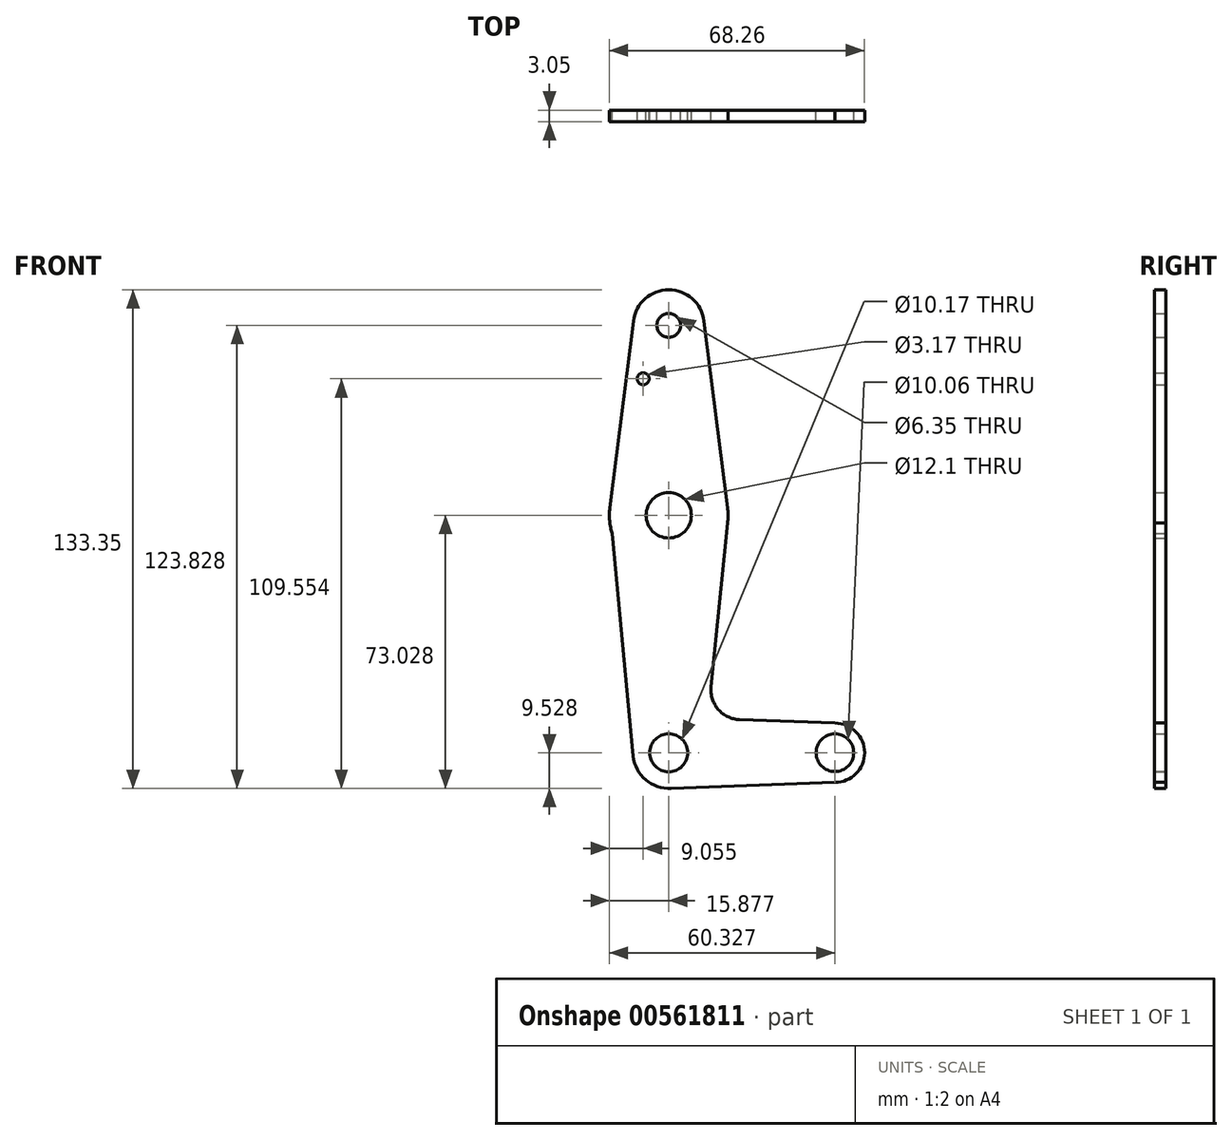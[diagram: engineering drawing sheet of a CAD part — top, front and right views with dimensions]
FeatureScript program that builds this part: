
annotation { "Feature Type Name" : "Feature", "Feature Type Description" : "" }
export const myFeature = defineFeature(function(context is Context, id is Id, definition is map)
    precondition{}
    {
        {
            var Q0;
            Q0=qCreatedBy(makeId("Front.planeOp"),FACE);
            var sketch = newSketch(context, id + "F0", { "sketchPlane" : qUnion([Q0])});
            skLineSegment(sketch, "E0", {"start": v(-18.2, 57.07) * mm, "end": v(-18.2, -57.23) * mm, "construction": true});
            skLineSegment(sketch, "E1", {"start": v(-18.2, -57.23) * mm, "end": v(26.26, -57.23) * mm, "construction": true});
            skCircle(sketch, "E2", {"center": v(-18.2, 57.07) * mm, "radius": 9.53 * mm});
            skCircle(sketch, "E3", {"center": v(-18.2, 6.27) * mm, "radius": 15.88 * mm});
            skCircle(sketch, "E4", {"center": v(-18.2, -57.23) * mm, "radius": 9.53 * mm});
            skCircle(sketch, "E5", {"center": v(26.26, -57.23) * mm, "radius": 7.94 * mm});
            skLineSegment(sketch, "E6", {"start": v(-27.64, 58.26) * mm, "end": v(-33.94, 8.25) * mm});
            skLineSegment(sketch, "E7", {"start": v(-8.74, 58.26) * mm, "end": v(-2.44, 8.25) * mm});
            skLineSegment(sketch, "E8", {"start": v(-33.94, 8.25) * mm, "end": v(-27.68, -58.13) * mm});
            skLineSegment(sketch, "E9", {"start": v(-2.44, 4.28) * mm, "end": v(-6.85, -39.64) * mm});
            skLineSegment(sketch, "E10", {"start": v(0.77, -48.38) * mm, "end": v(26.26, -49.3) * mm});
            skLineSegment(sketch, "E11", {"start": v(-18.2, -66.76) * mm, "end": v(26.26, -65.17) * mm});
            skCircle(sketch, "E12", {"center": v(-18.2, 57.07) * mm, "radius": 3.18 * mm});
            skCircle(sketch, "E13", {"center": v(-18.2, 6.27) * mm, "radius": 6.05 * mm});
            skCircle(sketch, "E14", {"center": v(-18.2, -57.23) * mm, "radius": 5.09 * mm});
            skCircle(sketch, "E15", {"center": v(26.26, -57.23) * mm, "radius": 5.03 * mm});
            skCircle(sketch, "E16", {"center": v(-25.02, 42.8) * mm, "radius": 1.59 * mm});
            skPoint(sketch, "E17.newPointA", {"position": v(-8.7, -58.13) * mm});
            skArc(sketch, "E17.filletArc", {"start": v(-6.85, -39.64) * mm, "mid": v(-4.93, -45.67) * mm, "end": v(0.77, -48.38) * mm});
            skSolve(sketch);
        }
        {
            var Q0;
            Q0 = qSketchRegion(id + "F0", true);
            extrude(context, id + "F1", {"entities" : qUnion([Q0]), "depth" : 3.05 * mm, "offsetDistance" : 25.4 * mm});
        }
    });
